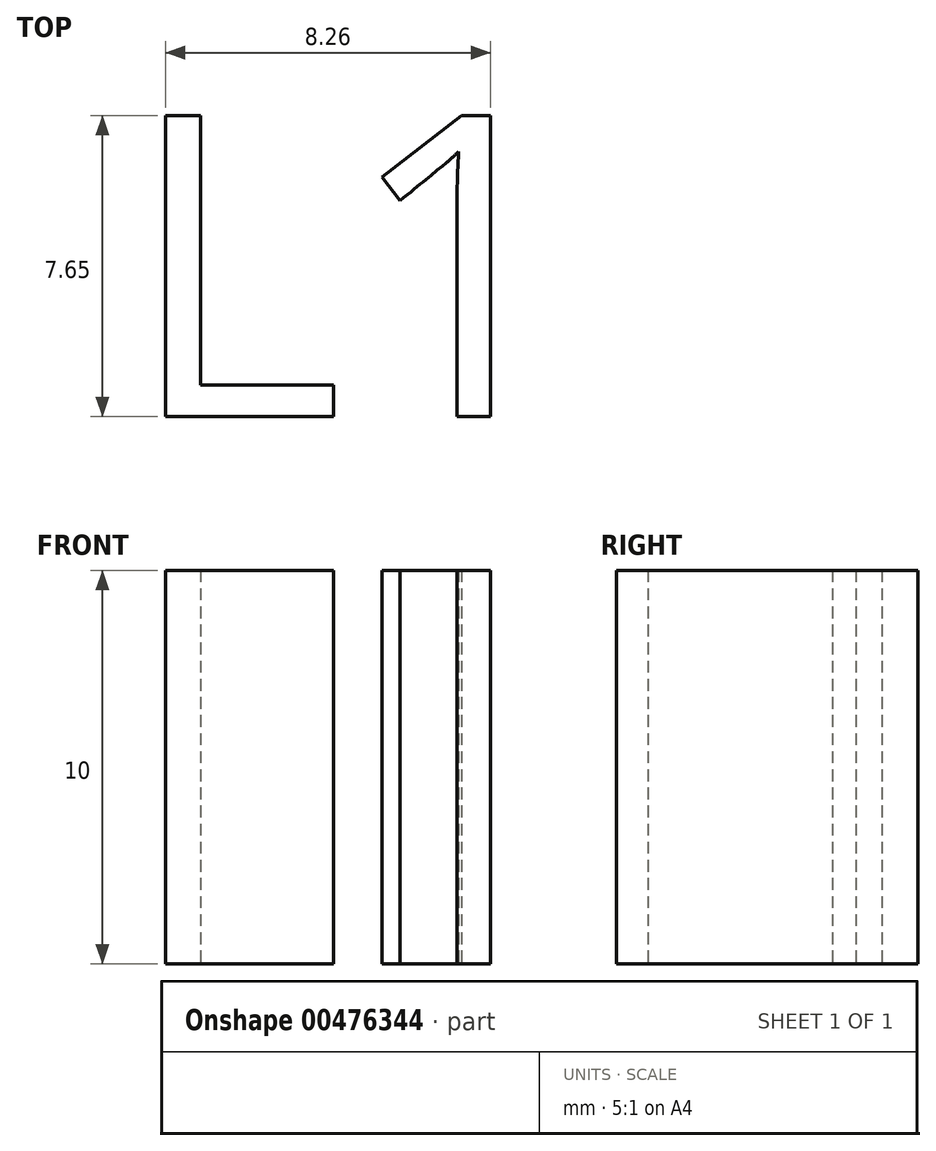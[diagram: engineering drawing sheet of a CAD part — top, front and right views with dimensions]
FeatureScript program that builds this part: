
annotation { "Feature Type Name" : "Feature", "Feature Type Description" : "" }
export const myFeature = defineFeature(function(context is Context, id is Id, definition is map)
    precondition{}
    {
        {
            var Q0;
            Q0=qCreatedBy(makeId("Top.planeOp"),FACE);
            var sketch = newSketch(context, id + "F0", { "sketchPlane" : qUnion([Q0])});
            skText(sketch, "E0", { "text": "L1\n", "fontName": "OpenSans-Regular.ttf"});
            skLineSegment(sketch, "E1", {"start": v(-5, 0) * mm, "end": v(5, 0) * mm, "construction": true});
            skLineSegment(sketch, "E2", {"start": v(0, 3.86) * mm, "end": v(0, -3.86) * mm, "construction": true});
            const initialGuessF0  = {"E0": [-0.005, -0.00386, 1, 0, 0.00772]};
            skSetInitialGuess(sketch, initialGuessF0);
            skSolve(sketch);
        }
        {
            var Q0;
            Q0 = qSketchRegion(id + "F0", true);
            extrude(context, id + "F1", {"entities" : qUnion([Q0]), "depth" : 10 * mm});
        }
    });
